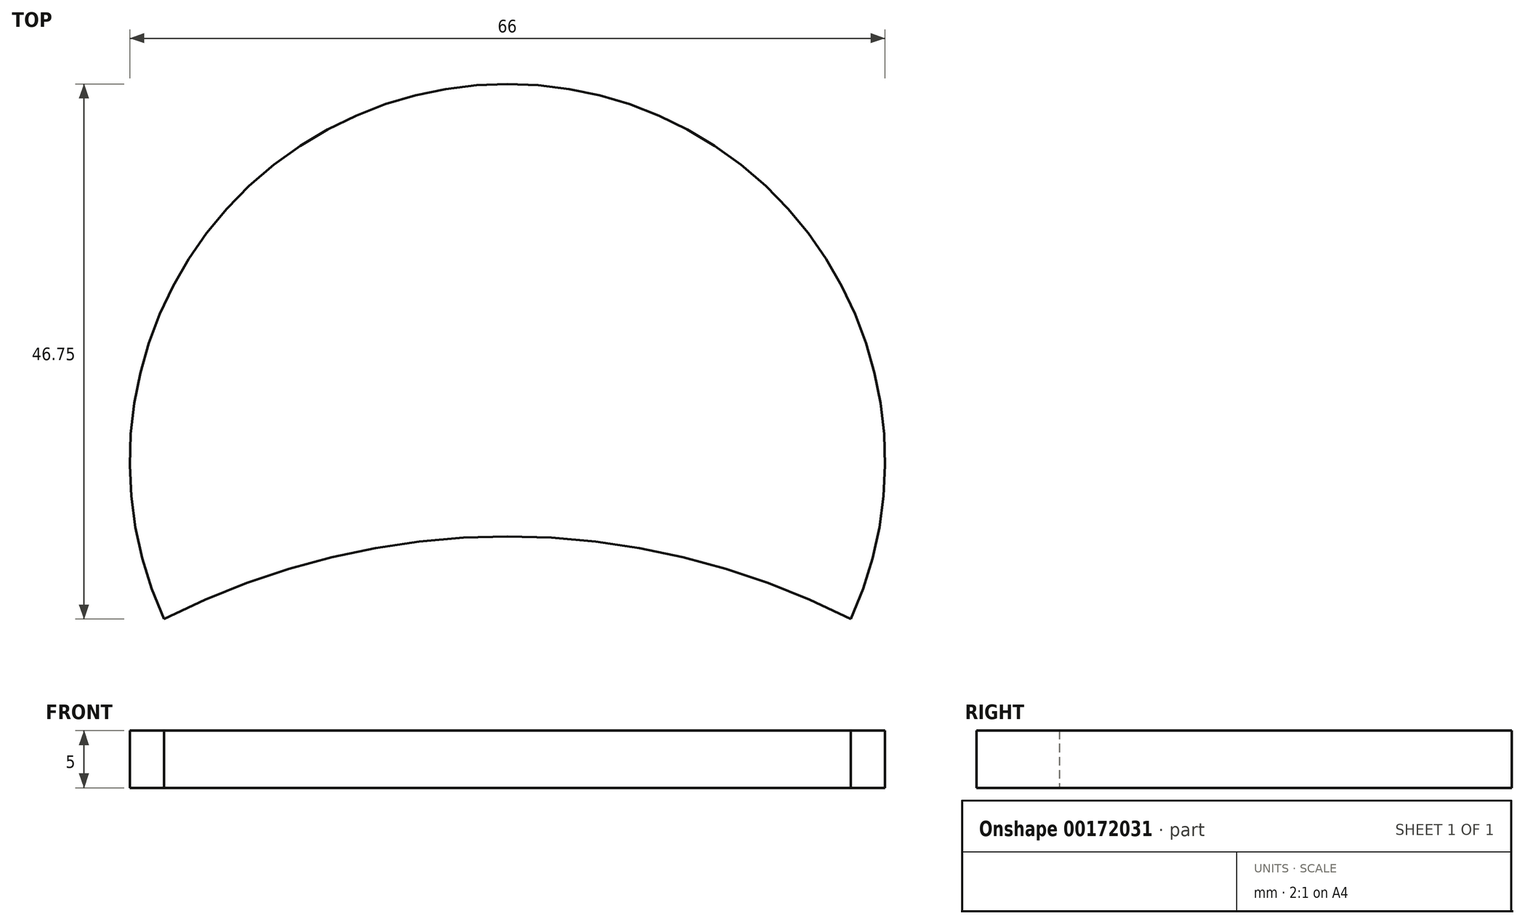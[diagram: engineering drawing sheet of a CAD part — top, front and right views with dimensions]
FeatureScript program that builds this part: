
annotation { "Feature Type Name" : "Feature", "Feature Type Description" : "" }
export const myFeature = defineFeature(function(context is Context, id is Id, definition is map)
    precondition{}
    {
        {
            var Q0;
            Q0=qCreatedBy(makeId("Top.planeOp"),FACE);
            var sketch = newSketch(context, id + "F0", { "sketchPlane" : qUnion([Q0])});
            skLineSegment(sketch, "E0.bottom", {"start": v(30, -11) * mm, "end": v(-30, -11) * mm});
            skLineSegment(sketch, "E0.top", {"start": v(30, 11) * mm, "end": v(-30, 11) * mm});
            skLineSegment(sketch, "E0.left", {"start": v(30, -11) * mm, "end": v(30, 11) * mm});
            skLineSegment(sketch, "E0.right", {"start": v(-30, -11) * mm, "end": v(-30, 11) * mm});
            skPoint(sketch, "E0.middle", {"position": v(0, 0) * mm});
            skLineSegment(sketch, "E1", {"start": v(-30, 0) * mm, "end": v(30, 0) * mm});
            skArc(sketch, "E2", {"start": v(30, 0) * mm, "mid": v(0, 46.75) * mm, "end": v(-30, 0) * mm});
            skArc(sketch, "E3", {"start": v(30, 0) * mm, "mid": v(0, 7.21) * mm, "end": v(-30, 0) * mm});
            skSolve(sketch);
        }
        {
            var Q0;
            {var subQ0=sQuery(id+"F0.wireOp",EDGE,"E0.top");Q0=makeQuery(id+"F0.imprint","IMPRINT",FACE,{"disambiguationData":[TD([[makeQuery(id+"F0.imprint","IMPRINT",EDGE,{"derivedFrom":subQ0}),1.0]])]});}
            var Q1;
            {var subQ0=sQuery(id+"F0.wireOp",EDGE,"E0.top");Q1=makeQuery(id+"F0.imprint","IMPRINT",FACE,{"disambiguationData":[TD([[makeQuery(id+"F0.imprint","IMPRINT",EDGE,{"derivedFrom":subQ0}),-1.0]])]});}
            extrude(context, id + "F1", {"entities" : qUnion([Q0, Q1]), "depth" : 5 * mm});
        }
    });
